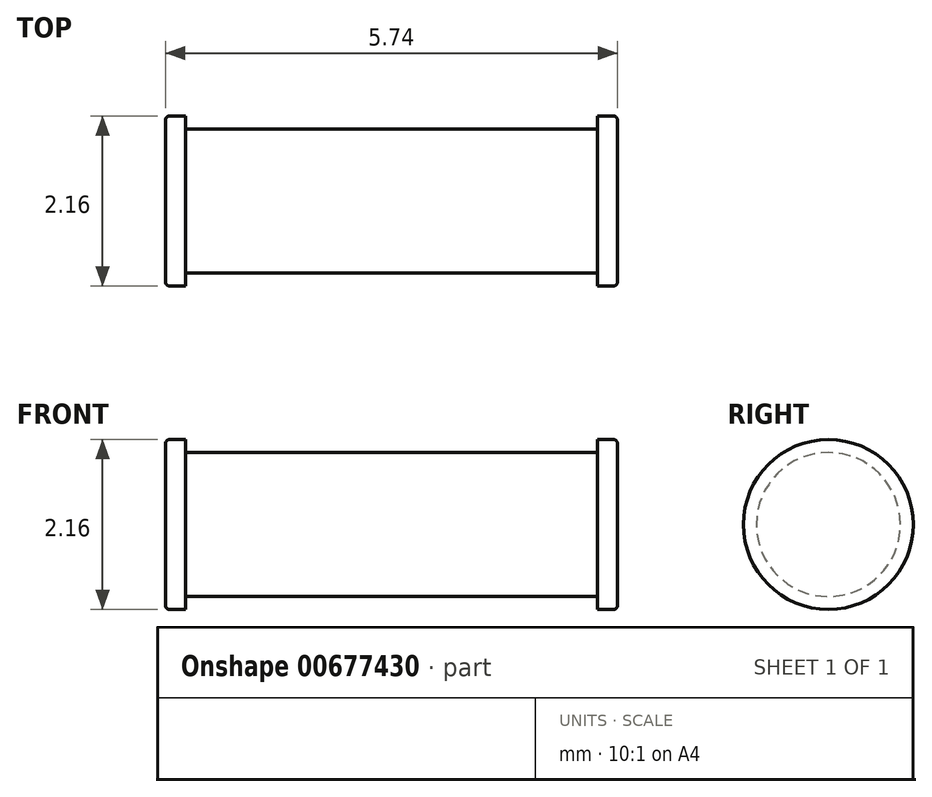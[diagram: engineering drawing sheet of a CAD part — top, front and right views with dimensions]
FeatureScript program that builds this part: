
annotation { "Feature Type Name" : "Feature", "Feature Type Description" : "" }
export const myFeature = defineFeature(function(context is Context, id is Id, definition is map)
    precondition{}
    {
        {
            var Q0;
            Q0=qCreatedBy(makeId("Right.planeOp"),FACE);
            var sketch = newSketch(context, id + "F0", { "sketchPlane" : qUnion([Q0])});
            skCircle(sketch, "E0", {"center": v(0, 0) * mm, "radius": 0.91 * mm});
            skSolve(sketch);
        }
        {
            var Q0;
            Q0 = qSketchRegion(id + "F0", true);
            extrude(context, id + "F1", {"entities" : qUnion([Q0]), "depth" : 2.62 * mm, "offsetDistance" : 25 * mm});
        }
        {
            var Q0;
            Q0=makeQuery(id+"F1.opExtrude","CAP_FACE",FACE,{"disambiguationData":[OSD([sQuery(id+"F0.wireOp",EDGE,"E0")])],"isStart":false});
            var sketch = newSketch(context, id + "F2", { "sketchPlane" : qUnion([Q0])});
            skCircle(sketch, "E1", {"center": v(0, 0) * mm, "radius": 1.08 * mm});
            skSolve(sketch);
        }
        {
            var Q0;
            Q0 = qSketchRegion(id + "F2", true);
            extrude(context, id + "F3", {"entities" : qUnion([Q0]), "operationType" : NewBodyOperationType.ADD, "depth" : 0.25 * mm, "offsetDistance" : 25 * mm});
        }
        {
            var Q0;
            Q0=makeQuery(id+"F3.opExtrude","CAP_EDGE",EDGE,{"disambiguationData":[OSD([sQuery(id+"F2.wireOp",EDGE,"E1")])],"isStart":false});
            fillet(context, id + "F4", {"entities" : qUnion([Q0]), "radius" : 0.05 * mm, "tangentPropagation" : true, "allowEdgeOverflow" : false});
        }
        {
            var Q0;
            Q0=makeQuery(id+"F1.opExtrude","SWEPT_BODY",BODY,{"disambiguationData":[OSD([sQuery(id+"F0.wireOp",EDGE,"E0")])]});
            var Q1;
            Q1=makeQuery(id+"F1.opExtrude","CAP_FACE",FACE,{"disambiguationData":[OSD([sQuery(id+"F0.wireOp",EDGE,"E0")])],"isStart":true});
            mirror(context, id + "F5", {"operationType" : NewBodyOperationType.ADD, "entities" : qUnion([Q0]), "mirrorPlane" : qUnion([Q1])});
        }
    });
